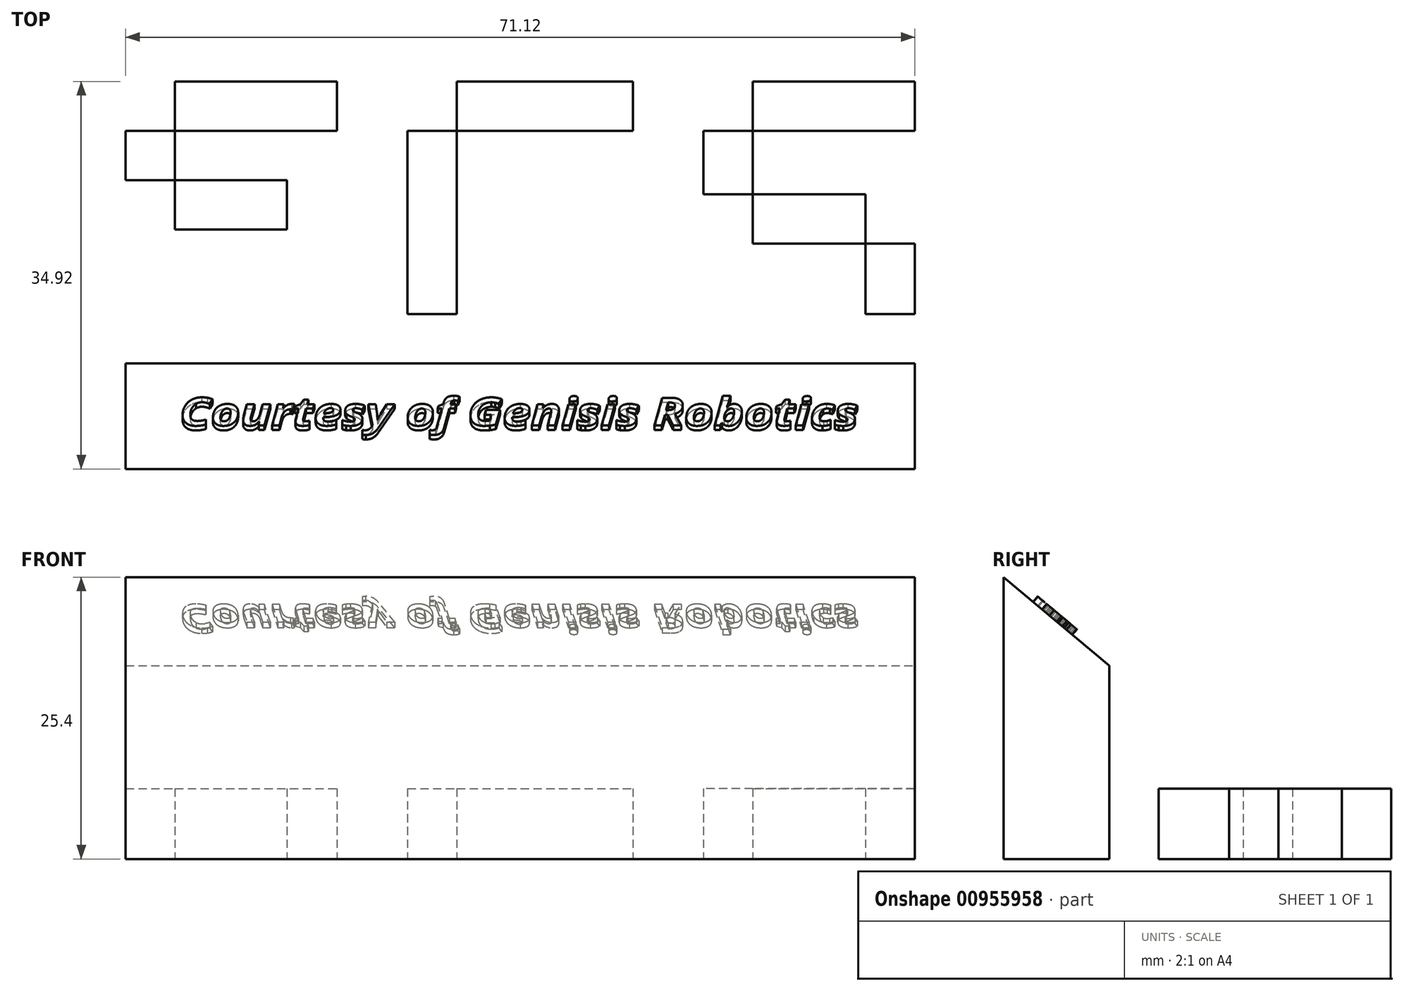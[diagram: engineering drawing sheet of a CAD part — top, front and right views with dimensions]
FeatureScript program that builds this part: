
annotation { "Feature Type Name" : "Feature", "Feature Type Description" : "" }
export const myFeature = defineFeature(function(context is Context, id is Id, definition is map)
    precondition{}
    {
        {
            var Q0;
            Q0=qCreatedBy(makeId("Top.planeOp"),FACE);
            var sketch = newSketch(context, id + "F0", { "sketchPlane" : qUnion([Q0])});
            skLineSegment(sketch, "E0.bottom", {"start": v(0, 0) * mm, "end": v(71.12, 0) * mm});
            skLineSegment(sketch, "E0.top", {"start": v(0, 9.53) * mm, "end": v(71.12, 9.53) * mm});
            skLineSegment(sketch, "E0.left", {"start": v(0, 0) * mm, "end": v(0, 9.53) * mm});
            skLineSegment(sketch, "E0.right", {"start": v(71.12, 0) * mm, "end": v(71.12, 9.53) * mm});
            skLineSegment(sketch, "E1.bottom", {"start": v(0, 9.53) * mm, "end": v(4.44, 9.53) * mm});
            skLineSegment(sketch, "E1.top", {"start": v(0, 34.93) * mm, "end": v(4.44, 34.93) * mm});
            skLineSegment(sketch, "E1.left", {"start": v(0, 9.53) * mm, "end": v(0, 34.93) * mm});
            skLineSegment(sketch, "E1.right", {"start": v(4.44, 9.53) * mm, "end": v(4.44, 34.92) * mm});
            skLineSegment(sketch, "E2.bottom", {"start": v(0, 34.93) * mm, "end": v(19.05, 34.93) * mm});
            skLineSegment(sketch, "E2.top", {"start": v(0, 30.48) * mm, "end": v(19.05, 30.48) * mm});
            skLineSegment(sketch, "E2.left", {"start": v(0, 34.93) * mm, "end": v(0, 30.48) * mm});
            skLineSegment(sketch, "E2.right", {"start": v(19.05, 34.92) * mm, "end": v(19.05, 30.48) * mm});
            skLineSegment(sketch, "E3.bottom", {"start": v(25.4, 9.53) * mm, "end": v(45.72, 9.53) * mm});
            skLineSegment(sketch, "E3.top", {"start": v(25.4, 13.97) * mm, "end": v(45.72, 13.97) * mm});
            skLineSegment(sketch, "E3.left", {"start": v(25.4, 9.53) * mm, "end": v(25.4, 13.97) * mm});
            skLineSegment(sketch, "E3.right", {"start": v(45.72, 9.53) * mm, "end": v(45.72, 13.97) * mm});
            skLineSegment(sketch, "E4.bottom", {"start": v(25.4, 9.53) * mm, "end": v(29.85, 9.53) * mm});
            skLineSegment(sketch, "E4.top", {"start": v(25.4, 34.93) * mm, "end": v(29.84, 34.93) * mm});
            skLineSegment(sketch, "E4.left", {"start": v(25.4, 9.53) * mm, "end": v(25.4, 34.93) * mm});
            skLineSegment(sketch, "E4.right", {"start": v(29.85, 9.53) * mm, "end": v(29.84, 34.93) * mm});
            skLineSegment(sketch, "E5.bottom", {"start": v(25.4, 34.92) * mm, "end": v(45.72, 34.92) * mm});
            skLineSegment(sketch, "E5.top", {"start": v(25.4, 30.48) * mm, "end": v(45.72, 30.48) * mm});
            skLineSegment(sketch, "E5.left", {"start": v(25.4, 34.93) * mm, "end": v(25.4, 30.48) * mm});
            skLineSegment(sketch, "E5.right", {"start": v(45.72, 34.93) * mm, "end": v(45.72, 30.48) * mm});
            skLineSegment(sketch, "E6.bottom", {"start": v(52.07, 9.53) * mm, "end": v(71.12, 9.53) * mm});
            skLineSegment(sketch, "E6.top", {"start": v(52.07, 13.97) * mm, "end": v(71.12, 13.97) * mm});
            skLineSegment(sketch, "E6.left", {"start": v(52.07, 9.53) * mm, "end": v(52.07, 13.97) * mm});
            skLineSegment(sketch, "E6.right", {"start": v(71.12, 9.53) * mm, "end": v(71.12, 13.97) * mm});
            skLineSegment(sketch, "E7.bottom", {"start": v(71.12, 9.53) * mm, "end": v(71.12, 9.53) * mm});
            skLineSegment(sketch, "E7.top", {"start": v(73.66, 24.77) * mm, "end": v(71.12, 24.77) * mm});
            skLineSegment(sketch, "E8.bottom", {"start": v(71.12, 24.77) * mm, "end": v(52.07, 24.77) * mm});
            skLineSegment(sketch, "E8.top", {"start": v(71.12, 20.32) * mm, "end": v(52.07, 20.32) * mm});
            skLineSegment(sketch, "E8.left", {"start": v(71.12, 24.77) * mm, "end": v(71.12, 20.32) * mm});
            skLineSegment(sketch, "E8.right", {"start": v(52.07, 24.77) * mm, "end": v(52.07, 20.32) * mm});
            skLineSegment(sketch, "E9.bottom", {"start": v(52.07, 20.32) * mm, "end": v(56.52, 20.32) * mm});
            skLineSegment(sketch, "E9.top", {"start": v(52.07, 34.93) * mm, "end": v(56.52, 34.93) * mm});
            skLineSegment(sketch, "E9.left", {"start": v(52.07, 20.32) * mm, "end": v(52.07, 34.93) * mm});
            skLineSegment(sketch, "E9.right", {"start": v(56.52, 20.32) * mm, "end": v(56.52, 34.93) * mm});
            skLineSegment(sketch, "E10.bottom", {"start": v(52.07, 34.93) * mm, "end": v(71.12, 34.93) * mm});
            skLineSegment(sketch, "E10.top", {"start": v(52.07, 30.48) * mm, "end": v(71.12, 30.48) * mm});
            skLineSegment(sketch, "E10.left", {"start": v(52.07, 34.93) * mm, "end": v(52.07, 30.48) * mm});
            skLineSegment(sketch, "E10.right", {"start": v(71.12, 34.93) * mm, "end": v(71.12, 30.48) * mm});
            skLineSegment(sketch, "E11.bottom", {"start": v(0, 26.03) * mm, "end": v(14.53, 26.03) * mm});
            skLineSegment(sketch, "E11.top", {"start": v(0, 21.59) * mm, "end": v(14.53, 21.59) * mm});
            skLineSegment(sketch, "E11.left", {"start": v(0, 26.03) * mm, "end": v(0, 21.59) * mm});
            skLineSegment(sketch, "E11.right", {"start": v(14.53, 26.03) * mm, "end": v(14.53, 21.59) * mm});
            skLineSegment(sketch, "E12.bottom", {"start": v(71.12, 24.77) * mm, "end": v(66.68, 24.77) * mm});
            skLineSegment(sketch, "E12.top", {"start": v(71.12, 9.53) * mm, "end": v(66.68, 9.53) * mm});
            skLineSegment(sketch, "E12.left", {"start": v(71.12, 24.77) * mm, "end": v(71.12, 9.53) * mm});
            skLineSegment(sketch, "E12.right", {"start": v(66.68, 24.77) * mm, "end": v(66.68, 9.53) * mm});
            skSolve(sketch);
        }
        {
            var Q0;
            {var subQ5=sQuery(id+"F0.wireOp",EDGE,"E2.right");Q0=makeQuery(id+"F0.imprint","IMPRINT",FACE,{"disambiguationData":[TD([[makeQuery(id+"F0.imprint","IMPRINT",EDGE,{"derivedFrom":subQ5}),-1.0]])]});}
            var Q1;
            {var subQ5=sQuery(id+"F0.wireOp",EDGE,"E2.left");Q1=makeQuery(id+"F0.imprint","IMPRINT",FACE,{"disambiguationData":[TD([[makeQuery(id+"F0.imprint","IMPRINT",EDGE,{"derivedFrom":subQ5}),1.0]])]});}
            var Q2;
            {var subQ3=sQuery(id+"F0.wireOp",EDGE,"E11.bottom");var subQ5=sQuery(id+"F0.wireOp",EDGE,"E1.right");var subQ6=makeQuery(id+"F0.imprint","INTERSECT",VERTEX,{"derivedFrom":[subQ5,subQ3]});Q2=makeQuery(id+"F0.imprint","IMPRINT",FACE,{"disambiguationData":[TD([[makeQuery(id+"F0.imprint","IMPRINT",EDGE,{"disambiguationData":[TD([[subQ6,-1.0]])],"derivedFrom":subQ5}),1.0]])]});}
            var Q3;
            {var subQ5=sQuery(id+"F0.wireOp",EDGE,"E11.left");Q3=makeQuery(id+"F0.imprint","IMPRINT",FACE,{"disambiguationData":[TD([[makeQuery(id+"F0.imprint","IMPRINT",EDGE,{"derivedFrom":subQ5}),1.0]])]});}
            var Q4;
            {var subQ5=sQuery(id+"F0.wireOp",EDGE,"E11.right");Q4=makeQuery(id+"F0.imprint","IMPRINT",FACE,{"disambiguationData":[TD([[makeQuery(id+"F0.imprint","IMPRINT",EDGE,{"derivedFrom":subQ5}),-1.0]])]});}
            var Q5;
            {var subQ0=sQuery(id+"F0.wireOp",EDGE,"E1.bottom");Q5=makeQuery(id+"F0.imprint","IMPRINT",FACE,{"disambiguationData":[TD([[makeQuery(id+"F0.imprint","IMPRINT",EDGE,{"derivedFrom":subQ0}),1.0]])]});}
            var Q6;
            {var subQ5=sQuery(id+"F0.wireOp",EDGE,"E5.right");Q6=makeQuery(id+"F0.imprint","IMPRINT",FACE,{"disambiguationData":[TD([[makeQuery(id+"F0.imprint","IMPRINT",EDGE,{"derivedFrom":subQ5}),-1.0]])]});}
            var Q7;
            {var subQ5=sQuery(id+"F0.wireOp",EDGE,"E4.bottom");Q7=makeQuery(id+"F0.imprint","IMPRINT",FACE,{"disambiguationData":[TD([[makeQuery(id+"F0.imprint","IMPRINT",EDGE,{"derivedFrom":subQ5}),1.0]])]});}
            var Q8;
            {var subQ0=sQuery(id+"F0.wireOp",EDGE,"E3.bottom");Q8=makeQuery(id+"F0.imprint","IMPRINT",FACE,{"disambiguationData":[TD([[makeQuery(id+"F0.imprint","IMPRINT",EDGE,{"derivedFrom":subQ0}),1.0]])]});}
            var Q9;
            {var subQ0=sQuery(id+"F0.wireOp",EDGE,"E4.left");var subQ1=sQuery(id+"F0.wireOp",EDGE,"E3.top");var subQ2=makeQuery(id+"F0.imprint","INTERSECT",VERTEX,{"derivedFrom":[subQ1,subQ0]});Q9=makeQuery(id+"F0.imprint","IMPRINT",FACE,{"disambiguationData":[TD([[makeQuery(id+"F0.imprint","IMPRINT",EDGE,{"disambiguationData":[TD([[subQ2,-1.0]])],"derivedFrom":subQ1}),1.0]])]});}
            var Q10;
            {var subQ5=sQuery(id+"F0.wireOp",EDGE,"E5.left");Q10=makeQuery(id+"F0.imprint","IMPRINT",FACE,{"disambiguationData":[TD([[makeQuery(id+"F0.imprint","IMPRINT",EDGE,{"derivedFrom":subQ5}),1.0]])]});}
            var Q11;
            {var subQ5=sQuery(id+"F0.wireOp",EDGE,"E10.left");Q11=makeQuery(id+"F0.imprint","IMPRINT",FACE,{"disambiguationData":[TD([[makeQuery(id+"F0.imprint","IMPRINT",EDGE,{"derivedFrom":subQ5}),1.0]])]});}
            var Q12;
            {var subQ5=sQuery(id+"F0.wireOp",EDGE,"E10.right");Q12=makeQuery(id+"F0.imprint","IMPRINT",FACE,{"disambiguationData":[TD([[makeQuery(id+"F0.imprint","IMPRINT",EDGE,{"derivedFrom":subQ5}),-1.0]])]});}
            var Q13;
            {var subQ0=sQuery(id+"F0.wireOp",EDGE,"E9.left");var subQ1=sQuery(id+"F0.wireOp",EDGE,"E8.bottom");var subQ2=makeQuery(id+"F0.imprint","INTERSECT",VERTEX,{"derivedFrom":[subQ1,subQ0]});Q13=makeQuery(id+"F0.imprint","IMPRINT",FACE,{"disambiguationData":[TD([[makeQuery(id+"F0.imprint","IMPRINT",EDGE,{"disambiguationData":[TD([[subQ2,1.0]])],"derivedFrom":subQ1}),-1.0]])]});}
            var Q14;
            {var subQ5=sQuery(id+"F0.wireOp",EDGE,"E9.bottom");Q14=makeQuery(id+"F0.imprint","IMPRINT",FACE,{"disambiguationData":[TD([[makeQuery(id+"F0.imprint","IMPRINT",EDGE,{"derivedFrom":subQ5}),1.0]])]});}
            var Q15;
            {var subQ1=sQuery(id+"F0.wireOp",EDGE,"E8.bottom");var subQ3=sQuery(id+"F0.wireOp",EDGE,"E9.right");var subQ4=makeQuery(id+"F0.imprint","INTERSECT",VERTEX,{"derivedFrom":[subQ1,subQ3]});Q15=makeQuery(id+"F0.imprint","IMPRINT",FACE,{"disambiguationData":[TD([[makeQuery(id+"F0.imprint","IMPRINT",EDGE,{"disambiguationData":[TD([[subQ4,1.0]])],"derivedFrom":subQ1}),1.0]])]});}
            var Q16;
            {var subQ5=sQuery(id+"F0.wireOp",EDGE,"E12.bottom");Q16=makeQuery(id+"F0.imprint","IMPRINT",FACE,{"disambiguationData":[TD([[makeQuery(id+"F0.imprint","IMPRINT",EDGE,{"derivedFrom":subQ5}),1.0]])]});}
            var Q17;
            {var subQ0=sQuery(id+"F0.wireOp",EDGE,"E12.left");var subQ1=sQuery(id+"F0.wireOp",EDGE,"E6.top");var subQ2=makeQuery(id+"F0.imprint","INTERSECT",VERTEX,{"derivedFrom":[subQ1,subQ0]});Q17=makeQuery(id+"F0.imprint","IMPRINT",FACE,{"disambiguationData":[TD([[makeQuery(id+"F0.imprint","IMPRINT",EDGE,{"disambiguationData":[TD([[subQ2,1.0]])],"derivedFrom":subQ1}),1.0]])]});}
            var Q18;
            {var subQ5=sQuery(id+"F0.wireOp",EDGE,"E12.top");Q18=makeQuery(id+"F0.imprint","IMPRINT",FACE,{"disambiguationData":[TD([[makeQuery(id+"F0.imprint","IMPRINT",EDGE,{"derivedFrom":subQ5}),-1.0]])]});}
            var Q19;
            {var subQ0=sQuery(id+"F0.wireOp",EDGE,"E6.bottom");Q19=makeQuery(id+"F0.imprint","IMPRINT",FACE,{"disambiguationData":[TD([[makeQuery(id+"F0.imprint","IMPRINT",EDGE,{"derivedFrom":subQ0}),1.0]])]});}
            extrude(context, id + "F1", {"entities" : qUnion([Q0, Q1, Q2, Q3, Q4, Q5, Q6, Q7, Q8, Q9, Q10, Q11, Q12, Q13, Q14, Q15, Q16, Q17, Q18, Q19]), "depth" : 6.35 * mm, "offsetDistance" : 25.4 * mm});
        }
        {
            var Q0;
            Q0=makeQuery(id+"F0.imprint","IMPRINT",FACE,{"disambiguationData":[TD([[makeQuery(id+"F0.imprint","IMPRINT",EDGE,{"derivedFrom":sQuery(id+"F0.wireOp",EDGE,"E0.bottom")}),1.0]])]});
            extrude(context, id + "F2", {"entities" : qUnion([Q0]), "depth" : 25.4 * mm, "offsetDistance" : 25.4 * mm});
        }
        {
            var Q0;
            Q0=makeQuery(id+"F2.opExtrude","SWEPT_FACE",FACE,{"disambiguationData":[OSD([sQuery(id+"F0.wireOp",EDGE,"E0.right")])]});
            var sketch = newSketch(context, id + "F3", { "sketchPlane" : qUnion([Q0])});
            skLineSegment(sketch, "E13", {"start": v(0, 25.4) * mm, "end": v(9.53, 17.4) * mm});
            skSolve(sketch);
        }
        {
            var Q0;
            {var subQ0=sQuery(id+"F3.wireOp",EDGE,"E13");Q0=makeQuery(id+"F3.imprint","IMPRINT",FACE,{"disambiguationData":[TD([[makeQuery(id+"F3.imprint","IMPRINT",EDGE,{"derivedFrom":subQ0}),1.0]])]});}
            extrude(context, id + "F4", {"entities" : qUnion([Q0]), "operationType" : NewBodyOperationType.REMOVE, "endBound" : BoundingType.THROUGH_ALL, "oppositeDirection" : true, "depth" : 25.4 * mm, "offsetDistance" : 25.4 * mm});
        }
        {
            var Q0;
            Q0=makeQuery(id+"F4.boolean.opBoolean","COPY",FACE,{"derivedFrom":makeQuery(id+"F4.opExtrude","SWEPT_FACE",FACE,{"disambiguationData":[OSD([sQuery(id+"F3.wireOp",EDGE,"E13")])]})});
            var sketch = newSketch(context, id + "F5", { "sketchPlane" : qUnion([Q0])});
            skText(sketch, "E14", { "text": "Courtesy of Genisis Robotics", "fontName": "OpenSans-BoldItalic.ttf"});
            skLineSegment(sketch, "E15", {"start": v(4.85, -10.1) * mm, "end": v(0, -10.1) * mm, "construction": true});
            skLineSegment(sketch, "E16", {"start": v(35.56, -8.46) * mm, "end": v(35.56, -3.9) * mm, "construction": true});
            const initialGuessF5  = {"E14": [0.00485, -0.01176, 1, 0, 0.0033]};
            skSetInitialGuess(sketch, initialGuessF5);
            skSolve(sketch);
        }
        {
            var Q0;
            Q0 = qSketchRegion(id + "F5", true);
            extrude(context, id + "F6", {"entities" : qUnion([Q0]), "operationType" : NewBodyOperationType.ADD, "depth" : 0.64 * mm, "offsetDistance" : 25.4 * mm});
        }
    });
